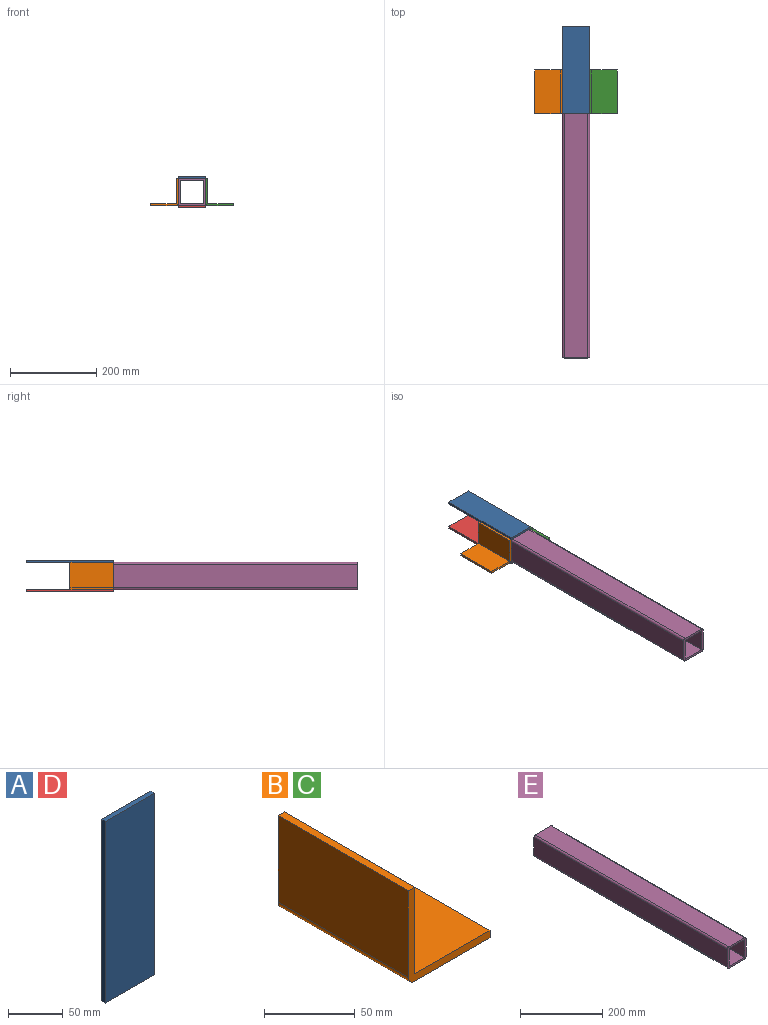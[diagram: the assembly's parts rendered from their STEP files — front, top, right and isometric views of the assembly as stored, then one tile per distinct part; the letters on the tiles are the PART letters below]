
ASSEMBLY  parts=5 mates=12
PART A: 6 faces, bbox 63.5x5x203.2 mm
  f0: plane 203.2x5mm, normal (-1,0,0), area 1016mm2, adj f1,f3,f4,f5
  f1: plane 63.5x5mm, normal (0,0,-1), area 317.5mm2, adj f0,f2,f4,f5
  f2: plane 203.2x5mm, normal (1,0,0), area 1016mm2, adj f1,f3,f4,f5
  f3: plane 63.5x5mm, normal (0,0,1), area 317.5mm2, adj f0,f2,f4,f5
  f4: plane 203.2x63.5mm, normal (0,-1,0), area 12903.2mm2, adj f0,f1,f2,f3
  f5: plane 203.2x63.5mm, normal (0,1,0), area 12903.2mm2, adj f0,f1,f2,f3
PART B: 9 faces, bbox 63.5x101.6x63.5 mm
  f0: plane 101.6x58.5mm, normal (-1,0,0), area 5943.6mm2, adj f1,f6,f7,f8
  f1: cylinder r=5mm len=101.6mm, axis (0,1,0), area 798mm2, adj f0,f2,f7,f8
  f2: plane 101.6x58.5mm, normal (0,0,-1), area 5943.6mm2, adj f1,f3,f7,f8
  f3: plane 101.6x5mm, normal (1,0,0), area 508mm2, adj f2,f4,f7,f8
  f4: plane 101.6x58.5mm, normal (0,0,1), area 5943.6mm2, adj f3,f5,f7,f8
  f5: plane 101.6x58.5mm, normal (1,0,0), area 5943.6mm2, adj f4,f6,f7,f8
  f6: plane 101.6x5mm, normal (0,0,1), area 508mm2, adj f0,f5,f7,f8
  f7: plane 63.5x63.5mm, normal (0,-1,0), area 604.6mm2, adj f0,f1,f2,f3,f4,f5,f6
  f8: plane 63.5x63.5mm, normal (0,1,0), area 604.6mm2, adj f0,f1,f2,f3,f4,f5,f6
PART C: same geometry as B
PART D: same geometry as A
PART E: 14 faces, bbox 63.5x666.1x63.5 mm
  f0: plane 666.1x53.5mm, normal (1,0,0), area 35636.4mm2, adj f1,f11,f12,f13
  f1: cylinder r=5mm len=666.1mm, axis (0,1,0), area 5231.5mm2, adj f0,f2,f12,f13
  f2: plane 666.1x53.5mm, normal (0,0,1), area 35636.4mm2, adj f1,f3,f12,f13
  f3: cylinder r=5mm len=666.1mm, axis (0,1,0), area 5231.5mm2, adj f2,f4,f12,f13
  f4: plane 666.1x53.5mm, normal (-1,0,0), area 35636.4mm2, adj f3,f5,f12,f13
  f5: cylinder r=5mm len=666.1mm, axis (0,1,0), area 5231.5mm2, adj f4,f6,f12,f13
  f6: plane 666.1x53.5mm, normal (0,0,-1), area 35636.4mm2, adj f5,f11,f12,f13
  f7: plane 666.1x53.5mm, normal (-1,0,0), area 35636.4mm2, adj f8,f10,f12,f13
  f8: plane 666.1x53.5mm, normal (0,0,1), area 35636.4mm2, adj f7,f9,f12,f13
  f9: plane 666.1x53.5mm, normal (1,0,0), area 35636.4mm2, adj f8,f10,f12,f13
  f10: plane 666.1x53.5mm, normal (0,0,-1), area 35636.4mm2, adj f7,f9,f12,f13
  f11: cylinder r=5mm len=666.1mm, axis (0,1,0), area 5231.5mm2, adj f0,f6,f12,f13
  f12: plane 63.5x63.5mm, normal (0,-1,0), area 1148.5mm2, adj f0,f1,f2,f3,f4,f5,f6,f7
  f13: plane 63.5x63.5mm, normal (0,1,0), area 1148.5mm2, adj f0,f1,f2,f3,f4,f5,f6,f7
PLACE A rot(axis=(-1,0,0),90deg) t=(-163.87,-619.69,-88.63)mm
PLACE B rot(axis=(0,-1,0),90deg) t=(-163.87,-518.09,-88.63)mm
PLACE C t=(-36.87,-518.09,-152.13)mm
PLACE D rot(axis=(-1,0,0),90deg) t=(-163.87,-619.69,-157.13)mm
PLACE E t=(-100.37,-518.09,-152.13)mm
MATE planar C.f2 <-> E.f6  axis (0,0,-1) through (-66.12,-568.89,-152.13)mm
MATE planar A.f5 <-> E.f2  axis (0,0,-1) through (-132.12,-619.69,-88.63)mm
MATE planar B.f2 <-> E.f4  axis (1,0,0) through (-163.87,-568.89,-117.88)mm
MATE planar E.f0 <-> C.f0  axis (1,0,0) through (-100.37,-851.14,-120.38)mm
MATE planar E.f13 <-> C.f8  axis (0,1,0) through (-132.12,-518.09,-120.38)mm
MATE planar D.f0 <-> E.f4  axis (-1,0,0) through (-163.87,-619.69,-157.13)mm
MATE planar E.f13 <-> B.f1  axis (0,1,0) through (-158.87,-518.09,-152.13)mm
MATE planar C.f7 <-> D.f1  axis (0,-1,0) through (-82.5,-619.69,-134.26)mm
MATE planar C.f7 <-> A.f1  axis (0,-1,0) through (-82.5,-619.69,-134.26)mm
MATE planar A.f2 <-> E.f0  axis (1,0,0) through (-100.37,-518.09,-86.13)mm
MATE planar D.f4 <-> E.f6  axis (0,0,1) through (-100.37,-518.09,-152.13)mm
MATE planar B.f0 <-> E.f6  axis (0,0,-1) through (-198.12,-568.89,-152.13)mm
